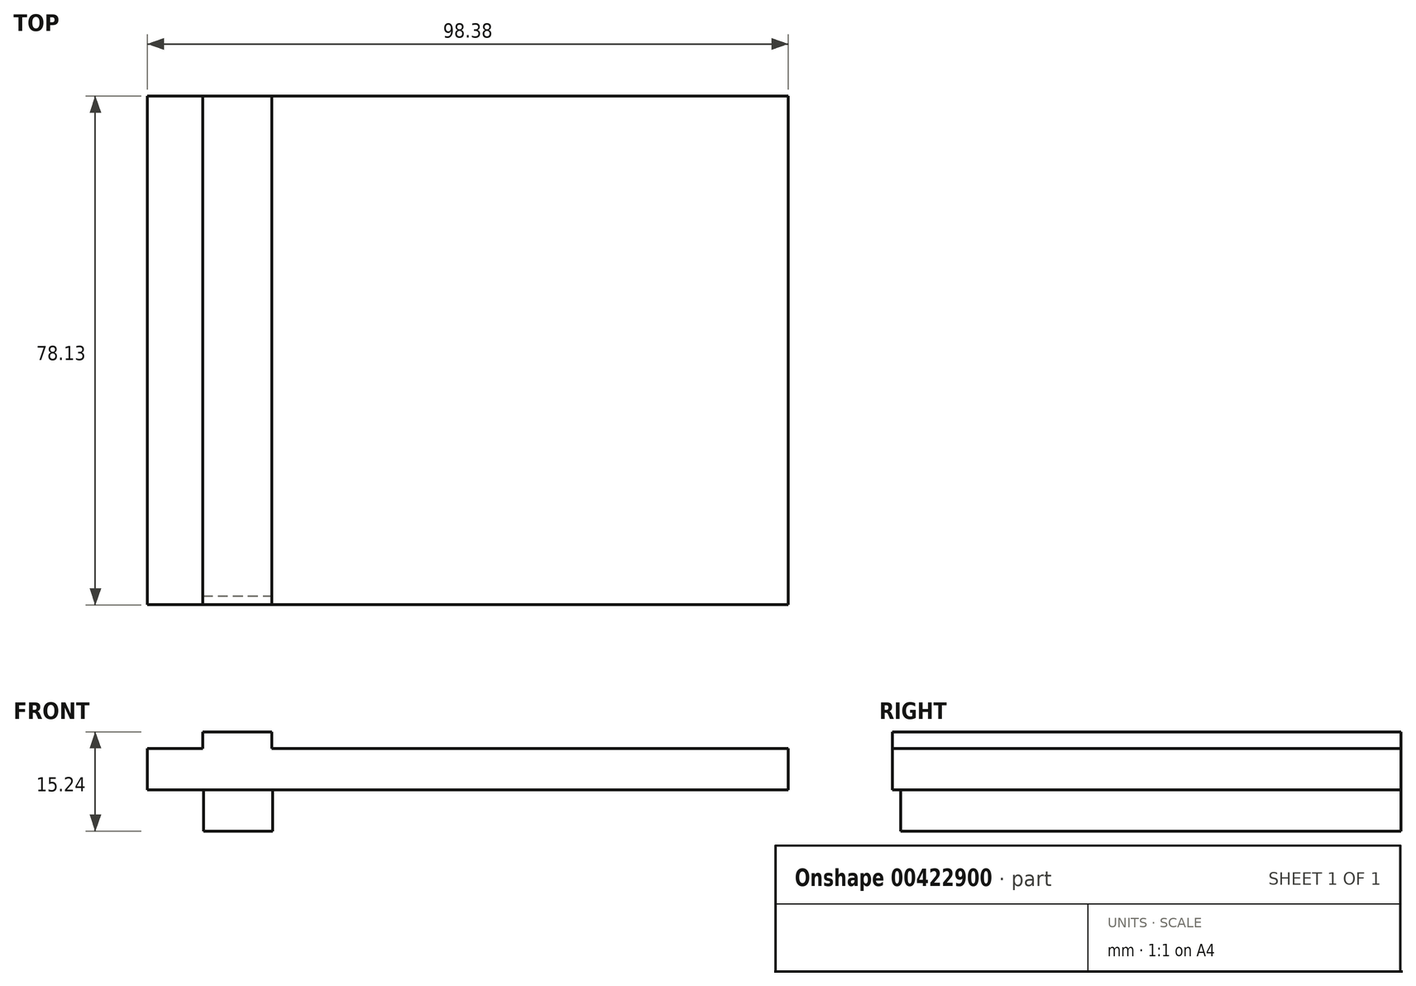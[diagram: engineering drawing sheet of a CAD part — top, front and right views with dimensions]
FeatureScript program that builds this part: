
annotation { "Feature Type Name" : "Feature", "Feature Type Description" : "" }
export const myFeature = defineFeature(function(context is Context, id is Id, definition is map)
    precondition{}
    {
        {
            var Q0;
            Q0=qCreatedBy(makeId("Top.planeOp"),FACE);
            var sketch = newSketch(context, id + "F0", { "sketchPlane" : qUnion([Q0])});
            skLineSegment(sketch, "E0.bottom", {"start": v(-46.4, -35.54) * mm, "end": v(51.98, -35.54) * mm});
            skLineSegment(sketch, "E0.top", {"start": v(-46.4, 42.59) * mm, "end": v(51.98, 42.59) * mm});
            skLineSegment(sketch, "E0.left", {"start": v(-46.4, -35.54) * mm, "end": v(-46.4, 42.59) * mm});
            skLineSegment(sketch, "E0.right", {"start": v(51.98, -35.54) * mm, "end": v(51.98, 42.59) * mm});
            skSolve(sketch);
        }
        {
            var Q0;
            Q0=makeQuery(id+"F0.imprint","IMPRINT",FACE,{"disambiguationData":[TD([[makeQuery(id+"F0.imprint","IMPRINT",EDGE,{"derivedFrom":sQuery(id+"F0.wireOp",EDGE,"E0.bottom")}),1.0]])]});
            extrude(context, id + "F1", {"entities" : qUnion([Q0]), "depth" : 2.54 * mm});
        }
        {
            var Q0;
            Q0=makeQuery(id+"F1.opExtrude","CAP_FACE",FACE,{"disambiguationData":[OSD([sQuery(id+"F0.wireOp",EDGE,"E0.bottom"),sQuery(id+"F0.wireOp",EDGE,"E0.top"),sQuery(id+"F0.wireOp",EDGE,"E0.left"),sQuery(id+"F0.wireOp",EDGE,"E0.right")])],"isStart":false});
            var sketch = newSketch(context, id + "F2", { "sketchPlane" : qUnion([Q0])});
            skLineSegment(sketch, "E1.bottom", {"start": v(-27.31, -35.54) * mm, "end": v(-37.89, -35.54) * mm});
            skLineSegment(sketch, "E1.top", {"start": v(-27.31, 42.59) * mm, "end": v(-37.89, 42.59) * mm});
            skLineSegment(sketch, "E1.left", {"start": v(-27.31, -35.54) * mm, "end": v(-27.31, 42.59) * mm});
            skLineSegment(sketch, "E1.right", {"start": v(-37.89, -35.54) * mm, "end": v(-37.89, 42.59) * mm});
            skSolve(sketch);
        }
        {
            var Q0;
            Q0 = qSketchRegion(id + "F2", true);
            var Q1;
            Q1=makeQuery(id+"F2.imprint","IMPRINT",FACE,{"disambiguationData":[TD([[makeQuery(id+"F2.imprint","IMPRINT",EDGE,{"derivedFrom":sQuery(id+"F2.wireOp",EDGE,"E1.bottom")}),1.0]])]});
            var Q2;
            Q2=makeQuery(id+"F1.opExtrude","CAP_FACE",FACE,{"disambiguationData":[OSD([sQuery(id+"F0.wireOp",EDGE,"E0.bottom"),sQuery(id+"F0.wireOp",EDGE,"E0.top"),sQuery(id+"F0.wireOp",EDGE,"E0.left"),sQuery(id+"F0.wireOp",EDGE,"E0.right")])],"isStart":true});
            extrude(context, id + "F3", {"entities" : qUnion([Q0, Q1, Q2]), "operationType" : NewBodyOperationType.ADD, "depth" : 6.35 * mm});
        }
        {
            var Q0;
            Q0=makeQuery(id+"F1.opExtrude","CAP_FACE",FACE,{"disambiguationData":[OSD([sQuery(id+"F0.wireOp",EDGE,"E0.bottom"),sQuery(id+"F0.wireOp",EDGE,"E0.top"),sQuery(id+"F0.wireOp",EDGE,"E0.left"),sQuery(id+"F0.wireOp",EDGE,"E0.right")])],"isStart":true});
            var sketch = newSketch(context, id + "F4", { "sketchPlane" : qUnion([Q0])});
            skSolve(sketch);
        }
        {
            var Q0;
            Q0=makeQuery(id+"F4.imprint","IMPRINT",FACE,{"disambiguationData":[TD([[makeQuery(id+"F4.imprint","IMPRINT",EDGE,{"derivedFrom":makeQuery(id+"F1.opExtrude","CAP_EDGE",EDGE,{"disambiguationData":[OSD([sQuery(id+"F0.wireOp",EDGE,"E0.bottom")])],"isStart":true})}),-1.0]])]});
            var sketch = newSketch(context, id + "F5", { "sketchPlane" : qUnion([Q0])});
            skLineSegment(sketch, "E2.bottom", {"start": v(-27.18, 34.23) * mm, "end": v(-37.8, 34.23) * mm});
            skLineSegment(sketch, "E2.top", {"start": v(-27.18, -42.56) * mm, "end": v(-37.8, -42.56) * mm});
            skLineSegment(sketch, "E2.left", {"start": v(-27.18, 34.23) * mm, "end": v(-27.18, -42.56) * mm});
            skLineSegment(sketch, "E2.right", {"start": v(-37.8, 34.23) * mm, "end": v(-37.8, -42.56) * mm});
            skSolve(sketch);
        }
        {
            var Q0;
            Q0=makeQuery(id+"F5.imprint","IMPRINT",FACE,{"disambiguationData":[TD([[makeQuery(id+"F5.imprint","IMPRINT",EDGE,{"derivedFrom":sQuery(id+"F5.wireOp",EDGE,"E2.bottom")}),1.0]])]});
            extrude(context, id + "F6", {"entities" : qUnion([Q0]), "operationType" : NewBodyOperationType.ADD, "depth" : 6.35 * mm});
        }
    });
